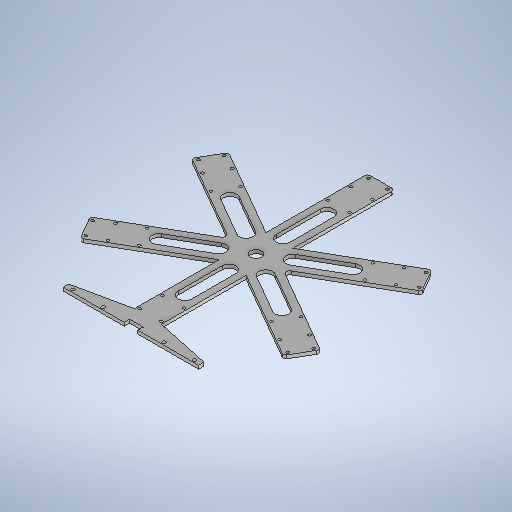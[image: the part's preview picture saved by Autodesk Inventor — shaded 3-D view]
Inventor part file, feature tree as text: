
AUTODESK INVENTOR PART (.ipt)
format: ipt  version: 2025.1 (Build 291241000, 241)  size: 568,320 bytes
history: native  units: mm
features: sketch x7, hole x3, extrude x2, fillet x1, projected_geometry x1
ambient origin geometry x8: Origin, YZ Plane, XZ Plane, XY Plane, X Axis, Y Axis, Z Axis, Center Point
bodies: Body1 (feature_tree)
feature tree (14):
  sketch  "Sketch1"  dims[d0=200.0mm d1=8.0mm d4=60.0deg]
  extrude  "Extrusion2"  Depth=8.0mm
  sketch  "Sketch3"  dims[d6=60.0deg d7=60.0deg]
  fillet  "Fillet1"  [1 undecoded]
  extrude  "Extrusion3"  TaperAngle=60.0deg  [1 undecoded]
  hole  "Hole4"  [1 undecoded]
  hole  "Hole5"  [1 undecoded]
  hole  "Hole6"  [1 undecoded]
  sketch  "Sketch8"  dims[d15=10.0mm d16=10.0mm d17=210.0mm d19=25.0mm d20=25.0mm d21=5.0mm d22=90.0deg d25=5.0mm d30=185.0mm d32=185.0mm d33=185.0mm d34=5.0mm d35=185.0mm d36=5.0mm d39=5.0mm d40=185.0mm d43=8.0mm d44=20.0mm d45=5.0mm d46=0.0mm d47=246.0mm d48=314.0mm d49=362.0mm d50=28.0mm d51=34.0mm d52=14.0mm d53=28.0mm d54=14.0mm d55=28.0mm d70=4.0mm d79=16.0mm d80=5.0mm d81=0.0mm d82=28.0mm d83=14.0mm d84=40.0mm d85=40.0mm d86=40.0mm d87=40.0mm d88=362.0mm d91=28.0mm d92=28.0mm d93=28.0mm d94=4.134mm d95=5.0mm d96=4.0mm d97=2.0mm d98=90.0deg d99=5.0mm d100=0.0mm d101=28.0mm d102=314.0mm d104=32.0mm d105=16.0mm d106=32.0mm d107=32.0mm d108=16.0mm d109=32.0mm d110=16.0mm d111=32.0mm d112=32.0mm d113=16.0mm d114=40.0mm d117=32.0mm d118=32.0mm d119=32.0mm d120=32.0mm d121=32.0mm d122=4.0mm d123=5.0mm d124=4.0mm d125=2.0mm d126=90.0deg d127=8.0mm d128=0.0mm d129=180.0mm d130=45.0mm d131=45.0mm d132=45.0mm d133=4.0mm d134=5.0mm d135=6.0mm d136=4.0mm d137=2.0mm d138=90.0deg d139=8.0mm d140=0.0mm d141=34.0mm d142=34.0mm d143=34.0mm d144=34.0mm d145=34.0mm d146=34.0mm d147=26.0mm]
  projected_geometry  "Projected Loop1"
  sketch  "Sketch4"  dims[d8=60.0deg d9=185.0mm]
  sketch  "Sketch5"  dims[d10=80.0mm d11=10.0mm]
  sketch  "Sketch6"  dims[d12=10.0mm d13=10.0mm]
  sketch  "Sketch7"  dims[d14=10.0mm]
note: 5 required parameter values undecoded (feature->parameter linkage not recoverable at this tier; creation-order binding heuristic only, values carry confidence <= 0.55)
